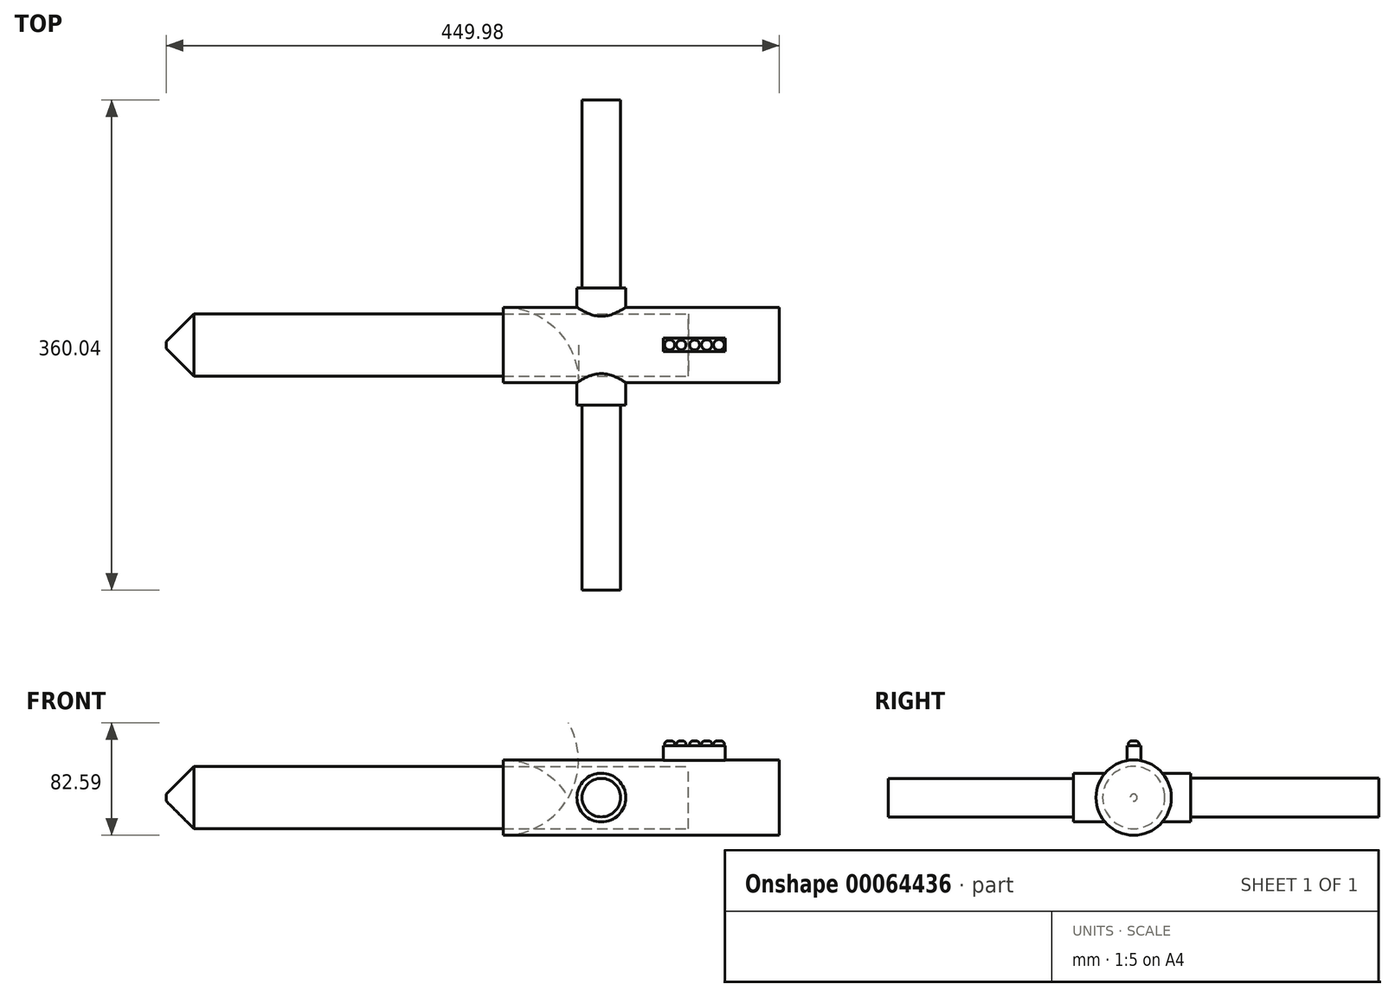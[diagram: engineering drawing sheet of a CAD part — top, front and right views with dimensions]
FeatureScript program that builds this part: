
annotation { "Feature Type Name" : "Feature", "Feature Type Description" : "" }
export const myFeature = defineFeature(function(context is Context, id is Id, definition is map)
    precondition{}
    {
        {
            var Q0;
            Q0=qCreatedBy(makeId("Front.planeOp"),FACE);
            var sketch = newSketch(context, id + "F0", { "sketchPlane" : qUnion([Q0])});
            skLineSegment(sketch, "E0", {"start": v(-88.2, 0) * mm, "end": v(66.62, 0) * mm});
            skLineSegment(sketch, "E1", {"start": v(66.62, 0) * mm, "end": v(66.62, 21.57) * mm});
            skLineSegment(sketch, "E2", {"start": v(66.62, 21.57) * mm, "end": v(66.62, 27.65) * mm});
            skLineSegment(sketch, "E3", {"start": v(66.62, 27.65) * mm, "end": v(66.62, 24.6) * mm});
            skLineSegment(sketch, "E4", {"start": v(66.62, 24.6) * mm, "end": v(71.2, 24.6) * mm});
            skLineSegment(sketch, "E5", {"start": v(71.2, 24.6) * mm, "end": v(71.2, 2.86) * mm});
            skLineSegment(sketch, "E6", {"start": v(71.2, 2.86) * mm, "end": v(66.62, 2.86) * mm});
            skLineSegment(sketch, "E7", {"start": v(66.62, 27.65) * mm, "end": v(-135.98, 27.65) * mm});
            skArc(sketch, "E8", {"start": v(-88.2, 0) * mm, "mid": v(-108.38, 20.24) * mm, "end": v(-135.98, 27.65) * mm});
            skSolve(sketch);
        }
        {
            var Q0;
            {var subQ3=sQuery(id+"F0.wireOp",EDGE,"E0");Q0=makeQuery(id+"F0.imprint","IMPRINT",FACE,{"disambiguationData":[TD([[makeQuery(id+"F0.imprint","IMPRINT",EDGE,{"derivedFrom":subQ3}),1.0]])]});}
            var Q1;
            Q1=sQuery(id+"F0.wireOp",EDGE,"E0");
            revolve(context, id + "F1", {"entities" : qUnion([Q0]), "axis" : qUnion([Q1]), "revolveType" : RevolveType.FULL});
        }
        {
            var Q0;
            Q0=qCreatedBy(makeId("Top.planeOp"),FACE);
            var sketch = newSketch(context, id + "F2", { "sketchPlane" : qUnion([Q0])});
            skLineSegment(sketch, "E9.bottom", {"start": v(-18.44, 5.15) * mm, "end": v(26.88, 5.15) * mm});
            skLineSegment(sketch, "E9.top", {"start": v(-18.44, -4.92) * mm, "end": v(26.88, -4.92) * mm});
            skLineSegment(sketch, "E9.left", {"start": v(-18.44, 5.15) * mm, "end": v(-18.44, -4.92) * mm});
            skLineSegment(sketch, "E9.right", {"start": v(26.88, 5.15) * mm, "end": v(26.88, -4.92) * mm});
            skSolve(sketch);
        }
        {
            var Q0;
            Q0 = qSketchRegion(id + "F2", true);
            extrude(context, id + "F3", {"entities" : qUnion([Q0]), "operationType" : NewBodyOperationType.ADD, "depth" : 38.03 * mm});
        }
        {
            var Q0;
            Q0=qCreatedBy(makeId("Top.planeOp"),FACE);
            var sketch = newSketch(context, id + "F4", { "sketchPlane" : qUnion([Q0])});
            skCircle(sketch, "E10", {"center": v(-13.87, 0) * mm, "radius": 3.74 * mm});
            skCircle(sketch, "E11", {"center": v(-5.4, 0) * mm, "radius": 3.53 * mm});
            skCircle(sketch, "E12", {"center": v(4.45, 0) * mm, "radius": 3.64 * mm});
            skCircle(sketch, "E13", {"center": v(13.38, 0) * mm, "radius": 3.85 * mm});
            skCircle(sketch, "E14", {"center": v(22.3, 0) * mm, "radius": 3.95 * mm});
            skSolve(sketch);
        }
        {
            var Q0;
            Q0 = qSketchRegion(id + "F4", true);
            extrude(context, id + "F5", {"entities" : qUnion([Q0]), "operationType" : NewBodyOperationType.ADD, "depth" : 41.65 * mm});
        }
        {
            var Q0;
            Q0=makeQuery(id+"F5.opExtrude","CAP_EDGE",EDGE,{"disambiguationData":[OSD([sQuery(id+"F4.wireOp",EDGE,"E14")])],"isStart":false});
            var Q1;
            Q1=makeQuery(id+"F5.opExtrude","CAP_EDGE",EDGE,{"disambiguationData":[OSD([sQuery(id+"F4.wireOp",EDGE,"E13")])],"isStart":false});
            var Q2;
            Q2=makeQuery(id+"F5.opExtrude","CAP_EDGE",EDGE,{"disambiguationData":[OSD([sQuery(id+"F4.wireOp",EDGE,"E12")])],"isStart":false});
            var Q3;
            Q3=makeQuery(id+"F5.opExtrude","CAP_EDGE",EDGE,{"disambiguationData":[OSD([sQuery(id+"F4.wireOp",EDGE,"E11")])],"isStart":false});
            var Q4;
            Q4=makeQuery(id+"F5.opExtrude","CAP_EDGE",EDGE,{"disambiguationData":[OSD([sQuery(id+"F4.wireOp",EDGE,"E10")])],"isStart":false});
            fillet(context, id + "F6", {"entities" : qUnion([Q0, Q1, Q2, Q3, Q4]), "radius" : 2.54 * mm, "tangentPropagation" : true, "allowEdgeOverflow" : false});
        }
        {
            var Q0;
            Q0=qCreatedBy(makeId("Front.planeOp"),FACE);
            var sketch = newSketch(context, id + "F7", { "sketchPlane" : qUnion([Q0])});
            skCircle(sketch, "E15", {"center": v(-64, 0) * mm, "radius": 17.89 * mm});
            skSolve(sketch);
        }
        {
            var Q0;
            Q0 = qSketchRegion(id + "F7", true);
            extrude(context, id + "F8", {"entities" : qUnion([Q0]), "operationType" : NewBodyOperationType.ADD, "depth" : 44.14 * mm, "hasSecondDirection" : true, "secondDirectionOppositeDirection" : true, "secondDirectionDepth" : 41.68 * mm});
        }
        {
            var Q0;
            Q0=makeQuery(id+"F8.opExtrude","CAP_FACE",FACE,{"disambiguationData":[OSD([sQuery(id+"F7.wireOp",EDGE,"E15")])],"isStart":true});
            var sketch = newSketch(context, id + "F9", { "sketchPlane" : qUnion([Q0])});
            skCircle(sketch, "E16", {"center": v(64, 0) * mm, "radius": 14.18 * mm});
            skSolve(sketch);
        }
        {
            var Q0;
            Q0 = qSketchRegion(id + "F9", true);
            extrude(context, id + "F10", {"entities" : qUnion([Q0]), "depth" : 138.28 * mm});
        }
        {
            var Q0;
            Q0=makeQuery(id+"F8.opExtrude","CAP_FACE",FACE,{"disambiguationData":[OSD([sQuery(id+"F7.wireOp",EDGE,"E15")])],"isStart":false});
            var sketch = newSketch(context, id + "F11", { "sketchPlane" : qUnion([Q0])});
            skCircle(sketch, "E17", {"center": v(-64, 0) * mm, "radius": 14.13 * mm});
            skSolve(sketch);
        }
        {
            var Q0;
            Q0 = qSketchRegion(id + "F11", true);
            extrude(context, id + "F12", {"entities" : qUnion([Q0]), "depth" : 135.94 * mm});
        }
        {
            var Q0;
            Q0=qCreatedBy(makeId("Right.planeOp"),FACE);
            var sketch = newSketch(context, id + "F13", { "sketchPlane" : qUnion([Q0])});
            skCircle(sketch, "E18", {"center": v(0, 0) * mm, "radius": 22.86 * mm});
            skSolve(sketch);
        }
        {
            var Q0;
            Q0 = qSketchRegion(id + "F13", true);
            extrude(context, id + "F14", {"entities" : qUnion([Q0]), "oppositeDirection" : true, "depth" : 383.36 * mm});
        }
        {
            var Q0;
            Q0=makeQuery(id+"F14.opExtrude","CAP_EDGE",EDGE,{"disambiguationData":[OSD([sQuery(id+"F13.wireOp",EDGE,"E18")])],"isStart":false});
            chamfer(context, id + "F15", {"entities" : qUnion([Q0]), "width" : 20.32 * mm, "tangentPropagation" : true});
        }
    });
